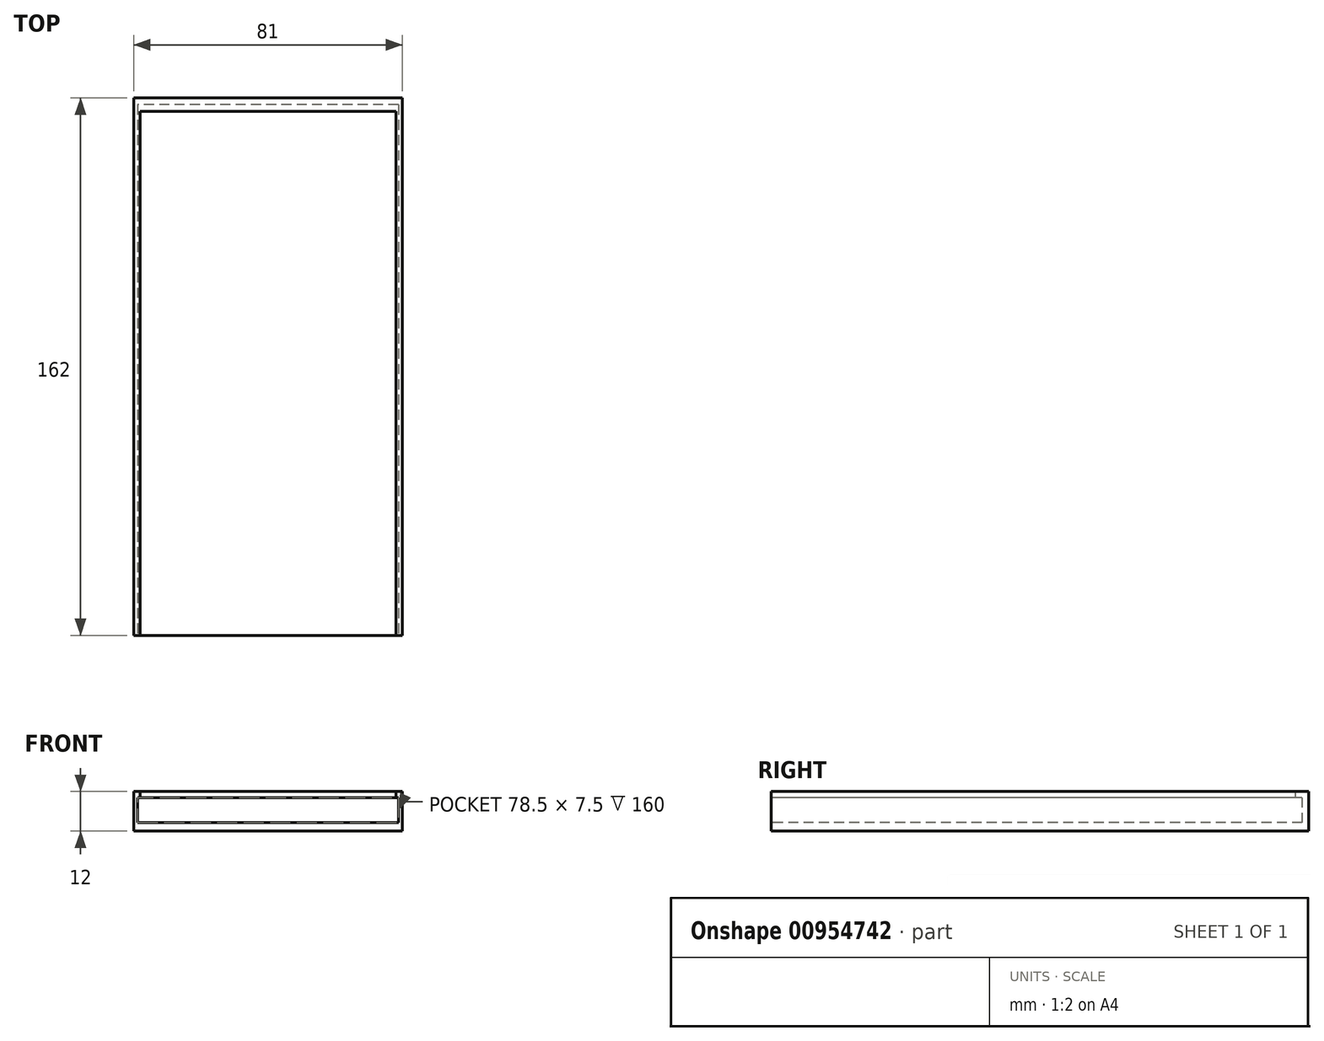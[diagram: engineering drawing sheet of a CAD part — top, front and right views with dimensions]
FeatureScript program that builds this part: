
annotation { "Feature Type Name" : "Feature", "Feature Type Description" : "" }
export const myFeature = defineFeature(function(context is Context, id is Id, definition is map)
    precondition{}
    {
        {
            var Q0;
            Q0=qCreatedBy(makeId("Top.planeOp"),FACE);
            var sketch = newSketch(context, id + "F0", { "sketchPlane" : qUnion([Q0])});
            skLineSegment(sketch, "E0.bottom", {"start": v(-73.04, 112.03) * mm, "end": v(7.96, 112.03) * mm});
            skLineSegment(sketch, "E0.top", {"start": v(-73.04, -49.97) * mm, "end": v(7.96, -49.97) * mm});
            skLineSegment(sketch, "E0.left", {"start": v(-73.04, 112.03) * mm, "end": v(-73.04, -49.97) * mm});
            skLineSegment(sketch, "E0.right", {"start": v(7.96, 112.03) * mm, "end": v(7.96, -49.97) * mm});
            skSolve(sketch);
        }
        {
            var Q0;
            Q0 = qSketchRegion(id + "F0", true);
            extrude(context, id + "F1", {"entities" : qUnion([Q0]), "depth" : 12 * mm, "offsetDistance" : 25 * mm});
        }
        {
            var Q0;
            Q0=makeQuery(id+"F1.opExtrude","SWEPT_FACE",FACE,{"disambiguationData":[OSD([sQuery(id+"F0.wireOp",EDGE,"E0.top")])]});
            var sketch = newSketch(context, id + "F2", { "sketchPlane" : qUnion([Q0])});
            skLineSegment(sketch, "E1.bottom", {"start": v(6.7, 10.12) * mm, "end": v(-71.8, 10.12) * mm});
            skLineSegment(sketch, "E1.top", {"start": v(6.7, 2.62) * mm, "end": v(-71.8, 2.62) * mm});
            skLineSegment(sketch, "E1.left", {"start": v(6.7, 10.12) * mm, "end": v(6.7, 2.62) * mm});
            skLineSegment(sketch, "E1.right", {"start": v(-71.8, 10.12) * mm, "end": v(-71.8, 2.62) * mm});
            skLineSegment(sketch, "E2", {"start": v(-71.8, 7.94) * mm, "end": v(-73.04, 7.94) * mm});
            skLineSegment(sketch, "E3", {"start": v(7.96, 7.66) * mm, "end": v(6.7, 7.66) * mm});
            skSolve(sketch);
        }
        {
            var Q0;
            Q0 = qSketchRegion(id + "F2", true);
            extrude(context, id + "F3", {"entities" : qUnion([Q0]), "operationType" : NewBodyOperationType.REMOVE, "oppositeDirection" : true, "depth" : 160 * mm, "offsetDistance" : 25 * mm});
        }
        {
            var Q0;
            Q0=makeQuery(id+"F1.opExtrude","CAP_FACE",FACE,{"disambiguationData":[OSD([sQuery(id+"F0.wireOp",EDGE,"E0.bottom"),sQuery(id+"F0.wireOp",EDGE,"E0.top"),sQuery(id+"F0.wireOp",EDGE,"E0.left"),sQuery(id+"F0.wireOp",EDGE,"E0.right")])],"isStart":false});
            var sketch = newSketch(context, id + "F4", { "sketchPlane" : qUnion([Q0])});
            skLineSegment(sketch, "E4.bottom", {"start": v(-71.04, 108.03) * mm, "end": v(5.96, 108.03) * mm});
            skLineSegment(sketch, "E4.top", {"start": v(-71.04, -49.97) * mm, "end": v(5.96, -49.97) * mm});
            skLineSegment(sketch, "E4.left", {"start": v(-71.04, 108.03) * mm, "end": v(-71.04, -49.97) * mm});
            skLineSegment(sketch, "E4.right", {"start": v(5.96, 108.03) * mm, "end": v(5.96, -49.97) * mm});
            skLineSegment(sketch, "E5", {"start": v(-71.04, -44.25) * mm, "end": v(-73.04, -44.25) * mm});
            skLineSegment(sketch, "E6", {"start": v(5.96, -43.88) * mm, "end": v(7.96, -43.88) * mm});
            skSolve(sketch);
        }
        {
            var Q0;
            Q0 = qSketchRegion(id + "F4", true);
            extrude(context, id + "F5", {"entities" : qUnion([Q0]), "operationType" : NewBodyOperationType.REMOVE, "oppositeDirection" : true, "depth" : 7.43 * mm, "offsetDistance" : 25 * mm});
        }
    });
